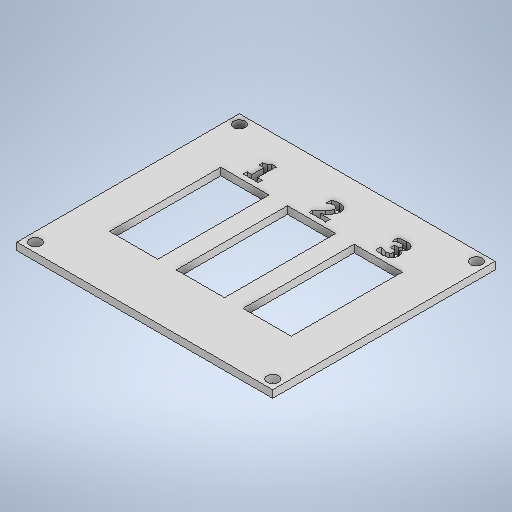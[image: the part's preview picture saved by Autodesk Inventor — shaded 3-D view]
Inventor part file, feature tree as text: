
AUTODESK INVENTOR PART (.ipt)
format: ipt  version: 2025 (Build 290162000, 162)  size: 340,992 bytes
history: native  units: mm
features: extrude x2, sketch x2, plane x1
ambient origin geometry x8: Origin, YZ Plane, XZ Plane, XY Plane, X Axis, Y Axis, Z Axis, Center Point
bodies: Solid1 (feature_tree)
feature tree (5):
  extrude  "Extrusion1"  Depth=60.0mm
  extrude  "Extrusion2"  Depth=13.0mm
  plane  "Work Plane2"
  sketch  "Sketch1"  dims[d0=69.0mm d1=60.0mm]
  sketch  "Sketch2"  dims[d2=2.0mm d3=0.0mm d4=13.0mm d5=30.0mm d6=2.0mm d7=0.0mm d8=5.0mm d9=1.0mm d10=8.0mm d13=5.0mm d15=3.1mm d16=2.5mm d17=2.5mm d18=2.5mm d19=2.5mm]
